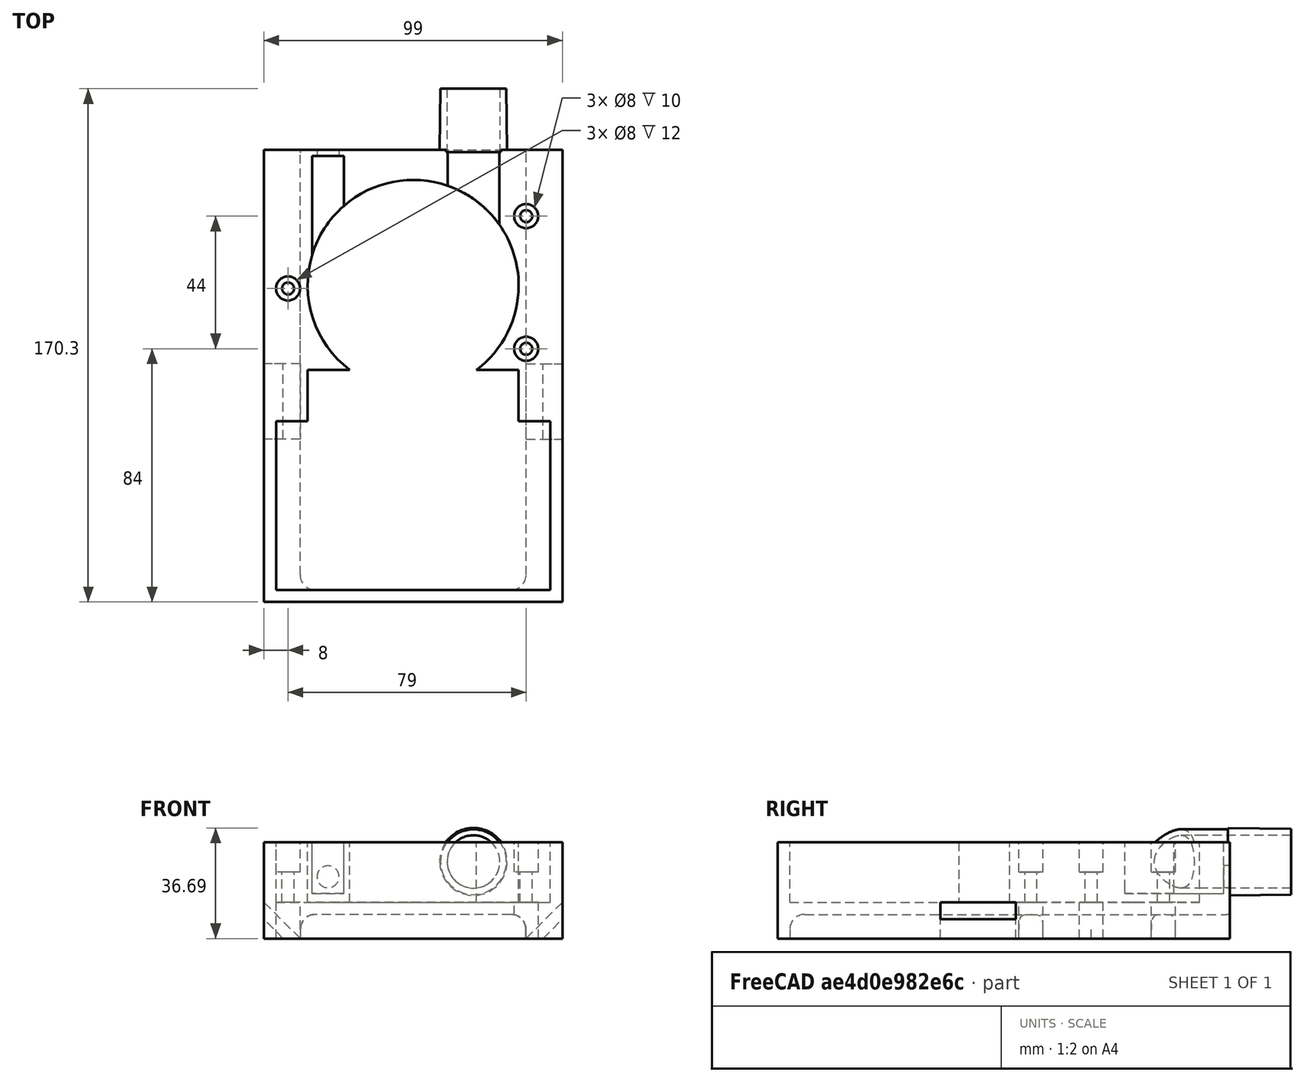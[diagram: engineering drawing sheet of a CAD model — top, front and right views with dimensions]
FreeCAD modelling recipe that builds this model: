
FCSTD DOCUMENT  (FreeCAD 0.18R4 (GitTag))
Label: blowermodel-v1
License: All rights reserved
LicenseURL: http://en.wikipedia.org/wiki/All_rights_reserved
objects: Part::Cylinder×17, Part::MultiFuse×11, Part::Box×7, Part::Fillet×6, Part::Cut×3, Part::Cone×2, Part::FeaturePython×1, Part::Mirroring×1
note: 48 computed .brp shape members not serialized (recipe doc carries the construction recipe); baked Part::Feature solids carry a one-line shape summary decoded from their .brp

FEATURE [Part::Cylinder] Cylinder  label="BlowerBody"
  Angle = 360
  AttacherType = Attacher::AttachEngine3D
  Height = 18
  Placement = pos=(0,0,4.5) rot=(0,0,1;0rad)
  Radius = 35
FEATURE [Part::Cylinder] Cylinder001  label="BlowerEndbearing"
  Angle = 360
  AttacherType = Attacher::AttachEngine3D
  Height = 5
  Placement = pos=(0,0,1) rot=(0,0,1;0rad)
  Radius = 2.25
FEATURE [Part::Cylinder] Cylinder002
  Angle = 360
  AttacherType = Attacher::AttachEngine3D
  Height = 10
  Placement = pos=(0,-28.4,0) rot=(0,0,1;0rad)
  Radius = 2
FEATURE [Part::FeaturePython] Array  label="BlowerFeet"  # Draft array (typed FeaturePython)
  Angle = 360
  ArrayType = 1
  Axis = (0,0,1)
  Base = -> Cylinder002
  Center = (0,0,0)
  Fuse = false
  IntervalAxis = (0,0,0)
  IntervalX = (1,0,0)
  IntervalY = (0,1,0)
  IntervalZ = (0,0,1)
  NumberPolar = 3
  NumberX = 1
  NumberY = 1
  NumberZ = 1
FEATURE [Part::Cylinder] Cylinder003  label="BlowerOutlet"
  Angle = 360
  AttacherType = Attacher::AttachEngine3D
  Height = 40
  Placement = pos=(20,36.3,13.5) rot=(1,0,0;1.5708rad)
  Radius = 8.75
FEATURE [Part::Cone] Cone  label="BlowerInlet"
  Angle = 360
  AttacherType = Attacher::AttachEngine3D
  Height = 13
  Placement = pos=(0,0,22.5) rot=(0,0,1;0rad)
  Radius1 = 27.25
  Radius2 = 27.15
FEATURE [Part::Cylinder] Cylinder004  label="BlowerBodyEnvelope"
  Angle = 360
  AttacherType = Attacher::AttachEngine3D
  Height = 25
  Radius = 35
FEATURE [Part::Cylinder] Cylinder005  label="OutletExtension"
  Angle = 360
  AttacherType = Attacher::AttachEngine3D
  Height = 40
  Placement = pos=(20,65.3,13.5) rot=(1,0,0;1.5708rad)
  Radius = 8.75
FEATURE [Part::Box] Box  label="DriverPocket"
  AttacherType = Attacher::AttachEngine3D
  Height = 20
  Length = 91
  Placement = pos=(-45.5,-106,0) rot=(0,0,1;0rad)
  Width = 56
FEATURE [Part::Box] Box001  label="WiringPocket"
  AttacherType = Attacher::AttachEngine3D
  Height = 20
  Length = 70
  Placement = pos=(-35,-53,0) rot=(0,0,1;0rad)
  Width = 20
FEATURE [Part::MultiFuse] Fusion  label="ElectronicsPocket"
  Placement = pos=(0,5,0) rot=(0,0,1;0rad)
  Shapes = -> [Box,Box001]
FEATURE [Part::Box] Box002  label="Potentiometer"
  AttacherType = Attacher::AttachEngine3D
  Height = 17
  Length = 10.5
  Placement = pos=(-30,18,5.5) rot=(0,0,1;0rad)
  Width = 35
FEATURE [Part::Cylinder] Cylinder006  label="Cylinder"
  Angle = 360
  AttacherType = Attacher::AttachEngine3D
  Height = 10
  Placement = pos=(-24.75,60.5,11) rot=(1,0,0;1.5708rad)
  Radius = 3.65
FEATURE [Part::MultiFuse] Fusion001  label="PotPocket"
  Placement = pos=(-3.5,-10,-2.5) rot=(0,0,1;0rad)
  Shapes = -> [Cylinder006,Box002]
FEATURE [Part::Box] Box003  label="Cube"
  AttacherType = Attacher::AttachEngine3D
  Height = 25
  Length = 75
  Placement = pos=(-37.5,-101,-29) rot=(0,0,1;0rad)
  Width = 150
FEATURE [Part::Fillet] Fillet
  Base = -> Box003
  Edges = 1 edges r=5: [Edge2]
FEATURE [Part::Fillet] Fillet001
  Base = -> Fillet
  Edges = 1 edges r=5: [Edge3]
FEATURE [Part::Fillet] Fillet002
  Base = -> Fillet001
  Edges = 1 edges r=5: [Edge17]
FEATURE [Part::Fillet] Fillet003
  Base = -> Fillet002
  Edges = 1 edges r=5: [Edge15]
FEATURE [Part::Fillet] Fillet004
  Base = -> Fillet003
  Edges = 1 edges r=5: [Edge18]
FEATURE [Part::Fillet] Fillet005  label="BatteryPocket"
  Base = -> Fillet004
  Edges = 4 edges r=5: [Edge3,Edge12,Edge13,Edge16]
FEATURE [Part::Box] Box004  label="HousingBlock"
  AttacherType = Attacher::AttachEngine3D
  Height = 32
  Length = 99
  Placement = pos=(-49.5,-105,-12) rot=(0,0,1;0rad)
  Width = 150
FEATURE [Part::Cylinder] Cylinder007  label="HousingOutlet"
  Angle = 360
  AttacherType = Attacher::AttachEngine3D
  Height = 40
  Placement = pos=(20,59.3,13.5) rot=(1,0,0;1.5708rad)
  Radius = 10.75
FEATURE [Part::MultiFuse] Fusion003  label="BlowerPocket"
  Shapes = -> [Cylinder004,Cone,Cylinder003,Array,Cylinder001,Cylinder]
FEATURE [Part::MultiFuse] Fusion004  label="CombinedPocket"
  Shapes = -> [Cylinder005,Fusion,Fusion001,Fillet005,Fusion003]
FEATURE [Part::Cone] Cone001  label="22mmTaper"
  Angle = 360
  AttacherType = Attacher::AttachEngine3D
  Height = 21
  Placement = pos=(20,65.3,13.5) rot=(0,-0.707107,0.707107;3.14159rad)
  Radius1 = 10.92
  Radius2 = 11.19
FEATURE [Part::MultiFuse] Fusion005  label="HousingLowerBody"
  Shapes = -> [Cone001,Cylinder007,Box004]
FEATURE [Part::Cut] Cut
  Base = -> Fusion005
  Tool = -> Fusion004
FEATURE [Part::Cylinder] Cylinder008  label="Cylinder003"
  Angle = 360
  AttacherType = Attacher::AttachEngine3D
  Height = 10
  Placement = pos=(-41.5,-1,10) rot=(0,0,1;0rad)
  Radius = 4
FEATURE [Part::Cylinder] Cylinder009  label="Cylinder004"
  Angle = 360
  AttacherType = Attacher::AttachEngine3D
  Height = 10
  Placement = pos=(37.5,-21,10) rot=(0,0,1;0rad)
  Radius = 4
FEATURE [Part::Cylinder] Cylinder010  label="Cylinder005"
  Angle = 360
  AttacherType = Attacher::AttachEngine3D
  Height = 10
  Placement = pos=(37.5,23,10) rot=(0,0,1;0rad)
  Radius = 4
FEATURE [Part::MultiFuse] Fusion006  label="TopMounting"
  Shapes = -> [Cylinder008,Cylinder009,Cylinder010]
FEATURE [Part::Cylinder] Cylinder011  label="Cylinder006"
  Angle = 360
  AttacherType = Attacher::AttachEngine3D
  Height = 30
  Placement = pos=(37.5,-21,10) rot=(0,0,1;0rad)
  Radius = 2
FEATURE [Part::Cylinder] Cylinder012  label="Cylinder007"
  Angle = 360
  AttacherType = Attacher::AttachEngine3D
  Height = 30
  Placement = pos=(37.5,23,10) rot=(0,0,1;0rad)
  Radius = 2
FEATURE [Part::Cylinder] Cylinder013  label="Cylinder008"
  Angle = 360
  AttacherType = Attacher::AttachEngine3D
  Height = 30
  Placement = pos=(-41.5,-1,10) rot=(0,0,1;0rad)
  Radius = 2
FEATURE [Part::MultiFuse] Fusion007  label="Mounting001"
  Placement = pos=(0,0,-30) rot=(0,0,1;0rad)
  Shapes = -> [Cylinder013,Cylinder011,Cylinder012]
FEATURE [Part::Cylinder] Cylinder014  label="Cylinder009"
  Angle = 360
  AttacherType = Attacher::AttachEngine3D
  Height = 20
  Placement = pos=(37.5,-21,10) rot=(0,0,1;0rad)
  Radius = 4
FEATURE [Part::Cylinder] Cylinder015  label="Cylinder010"
  Angle = 360
  AttacherType = Attacher::AttachEngine3D
  Height = 20
  Placement = pos=(37.5,23,10) rot=(0,0,1;0rad)
  Radius = 4
FEATURE [Part::Cylinder] Cylinder016  label="Cylinder011"
  Angle = 360
  AttacherType = Attacher::AttachEngine3D
  Height = 20
  Placement = pos=(-41.5,-1,10) rot=(0,0,1;0rad)
  Radius = 4
FEATURE [Part::MultiFuse] Fusion008  label="Mounting002"
  Placement = pos=(0,0,-30) rot=(0,0,1;0rad)
  Shapes = -> [Cylinder016,Cylinder014,Cylinder015]
FEATURE [Part::MultiFuse] Fusion009  label="BottomMounting"
  Shapes = -> [Fusion007,Fusion008]
FEATURE [Part::MultiFuse] Fusion010  label="CombinedMounting"
  Shapes = -> [Fusion006,Fusion009]
FEATURE [Part::Cut] Cut001
  Base = -> Cut
  Tool = -> Fusion010
FEATURE [Part::Box] Box005  label="Slot1"
  AttacherType = Attacher::AttachEngine3D
  Height = 4
  Length = 25
  Placement = pos=(-37.4228,-51,-17.6777) rot=(0.357407,0.357407,0.862856;1.71777rad)
  Width = 40
FEATURE [Part::Box] Box006  label="Slot2"
  AttacherType = Attacher::AttachEngine3D
  Height = 4
  Length = 25
  Placement = pos=(-37.4228,-44,-17.6777) rot=(0.357407,0.357407,0.862856;1.71777rad)
  Width = 40
FEATURE [Part::Mirroring] Part__Mirroring  label="Slot2 (Mirror #1)"
  Base = (0,0,0)
  Normal = (1,0,0)
  Placement = pos=(0,-7,0) rot=(0,0,1;0rad)
  Source = -> Box006
FEATURE [Part::MultiFuse] Fusion011  label="StrapSlots"
  Shapes = -> [Box005,Part__Mirroring]
FEATURE [Part::Cut] Cut002  label="PAPR-Lower-Housing"
  Base = -> Cut001
  Tool = -> Fusion011
